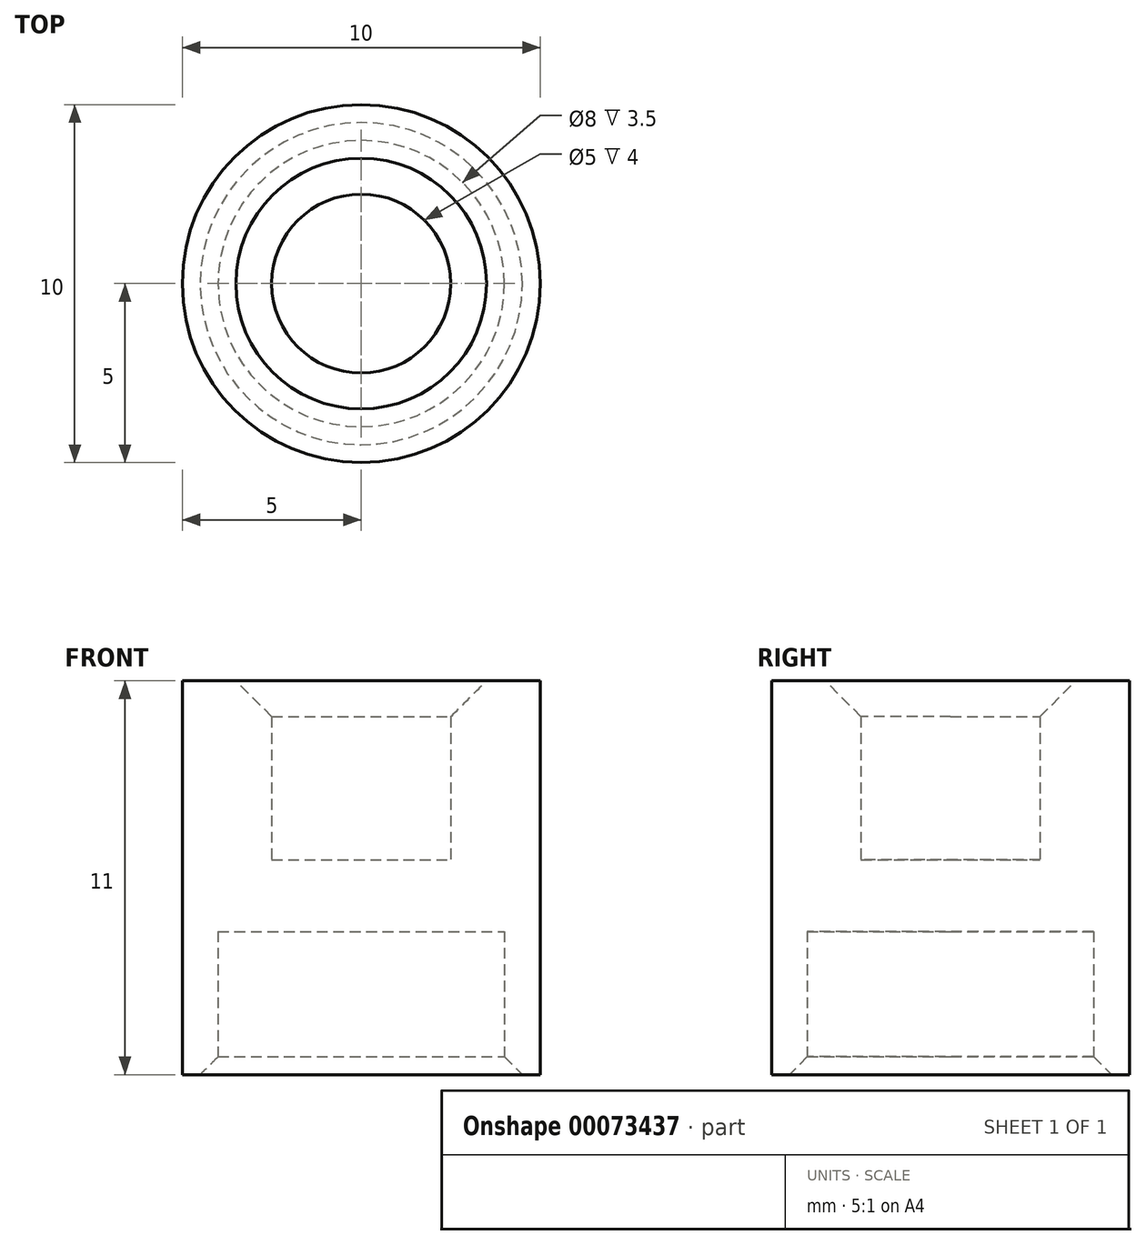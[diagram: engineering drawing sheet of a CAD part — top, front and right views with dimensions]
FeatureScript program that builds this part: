
annotation { "Feature Type Name" : "Feature", "Feature Type Description" : "" }
export const myFeature = defineFeature(function(context is Context, id is Id, definition is map)
    precondition{}
    {
        {
            var Q0;
            Q0=qCreatedBy(makeId("Front.planeOp"),FACE);
            var sketch = newSketch(context, id + "F0", { "sketchPlane" : qUnion([Q0])});
            skLineSegment(sketch, "E0", {"start": v(0, 0) * mm, "end": v(0, 4) * mm, "construction": true});
            skLineSegment(sketch, "E1", {"start": v(4, 0) * mm, "end": v(5, 0) * mm});
            skLineSegment(sketch, "E2", {"start": v(5, 0) * mm, "end": v(5, 11) * mm});
            skLineSegment(sketch, "E3", {"start": v(5, 11) * mm, "end": v(2.5, 11) * mm});
            skLineSegment(sketch, "E4", {"start": v(2.5, 11) * mm, "end": v(2.5, 6) * mm});
            skLineSegment(sketch, "E5", {"start": v(2.5, 6) * mm, "end": v(0, 6) * mm});
            skLineSegment(sketch, "E6", {"start": v(0, 6) * mm, "end": v(0, 4) * mm});
            skLineSegment(sketch, "E7", {"start": v(0, 4) * mm, "end": v(4, 4) * mm});
            skLineSegment(sketch, "E8", {"start": v(4, 4) * mm, "end": v(4, 0) * mm});
            skSolve(sketch);
        }
        {
            var Q0;
            Q0=qSketchRegion(id+"F0",true);
            var Q1;
            Q1=sQuery(id+"F0.wireOp",EDGE,"E0");
            revolve(context, id + "F1", {"entities" : qUnion([Q0]), "axis" : qUnion([Q1]), "revolveType" : RevolveType.FULL});
        }
        {
            var Q0;
            Q0=makeQuery(id+"F1.opRevolve","SWEPT_EDGE",EDGE,{"disambiguationData":[OSD([sQuery(id+"F0.wireOp",EDGE,"E3"),sQuery(id+"F0.wireOp",EDGE,"E4")])]});
            chamfer(context, id + "F2", {"entities" : qUnion([Q0]), "width" : 1 * mm, "tangentPropagation" : true});
        }
        {
            var Q0;
            Q0=makeQuery(id+"F1.opRevolve","SWEPT_EDGE",EDGE,{"disambiguationData":[OSD([sQuery(id+"F0.wireOp",EDGE,"E1"),sQuery(id+"F0.wireOp",EDGE,"E8")])]});
            chamfer(context, id + "F3", {"entities" : qUnion([Q0]), "width" : 0.5 * mm, "tangentPropagation" : true});
        }
    });
